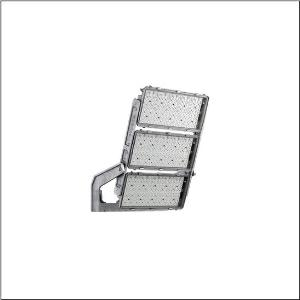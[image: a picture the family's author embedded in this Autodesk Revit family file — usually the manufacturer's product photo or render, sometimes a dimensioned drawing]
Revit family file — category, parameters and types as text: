
# Revit family: floodlight_fl_11_maxi_pro_remote___pl43_5xa779426a01aa_52e7
name_source: partatom
category: Lighting Fixtures
units: mm (PartAtom-declared; Revit-internal decimal feet)

## family parameters
Cut with Voids When Loaded = No
Host = Face
Light Source = No
Part Type = Normal
Room Calculation Point = No
Round Connector Dimension = Use Diameter
Shared = No

## types (1)
- --- (1 x LED, 172790 lm, 1387.6 W, 4000K)
    Apparent Load = 1388 VA
    CIE Flux Codes = 25 74 99 100 100
    Color Rendering = 70
    Color Temperature = 4000K
    Default Elevation = 1800 mm
    Description = Floodlight FL 11  maxi  pro Remote floodlight; light control with lens of PMMA; cover panel of toughened safety glass, transparent; light distribution: PL43, asymmetric direct distribution, LEDcolour temperature: 4000K, rated luminous flux: 172.790lm, colour rendering: CRI > 70, light colour: 740; luminous efficacy: 125lm/W; brightness control: DALI 2 (1 DALI address); with terminal, 8-pole, max. 2.5mm², mains connection: 220..240V/380..400V AC, 50/60Hz, surge voltage resistance: line to ground: 10kV, ECG replaceable separately, LED unit replaceable without ESD environment, dustproof LED module, dimming range 10..100%, no afterglow with DALI off / DMX off command; 1388W floodlight with 2x LED unit of diecast aluminium, coated grey; length: 713mm / width: 651mm / height: 338mm; mounting bracket, of diecast aluminium, uncoated, natural, equipment: Power, protection rating (complete): IP66; insulation class (complete): insulation class I (protective earthing); certification: CE, ENEC, VDE; ball protection: ball impact resistance with accessories, impact resistance: IK07; rated ambient temperature 10°C, only for outdoor installations, permissible operating ambient temperature: -40..+30°C, permissible storage temperature: -40..+85°C; packaging unit: 1 piece

Light Distribution: PL43
    Height = 320 mm
    Lamp = 1 x LED
    Lamp Light Flux = 172790 lm
    Lamp Power = 1387.6 W
    Lamp count = 1
    Length = 1002 mm
    Luminous efficacy = 125 lm/W
    Manufacturer = Siteco
    ModVariant = No
    Model = 5XA779426A01AA
    Mounting Place = Ceiling
    Mounting Type = Surface mounted
    Number of Poles = 1
    OnlyDefault = Yes
    Power Factor = 1
    Product Name = Floodlight FL 11 maxi pro Remote | PL43
    Product group = floodlight | ceiling mounted
    ProductGroupID = 303
    Protection Class = Protection class I
    Protection Degree = IP 66
    RLX_Detail_Level = 1
    RLX_Emergency_Light_Flux = 0 lm
    RLX_Emergency_Type = 0
    RLX_Emergency_Type_DB = No
    RlxData = <blob elided: 52245 chars, md5=0ba741a3>
    Socket = socket
    Standby Power = 0 W
    System Light Flux = 172790 lm
    System Power = 1388 W
    Type Comments = factory setting: luminous flux: 100 % | dim-lin: 254 | 955 mA
    Type Image = l_1006784.jpg
    URL = http://relux.com
    VarID = @adj_045005
    Voltage = 0 V
    Weight = 0.00 kg
    Width = 655 mm

## geometry (parser evidence)
native form markers: Blend x4, Sweep x14
no freeform markers — native parametric forms only
